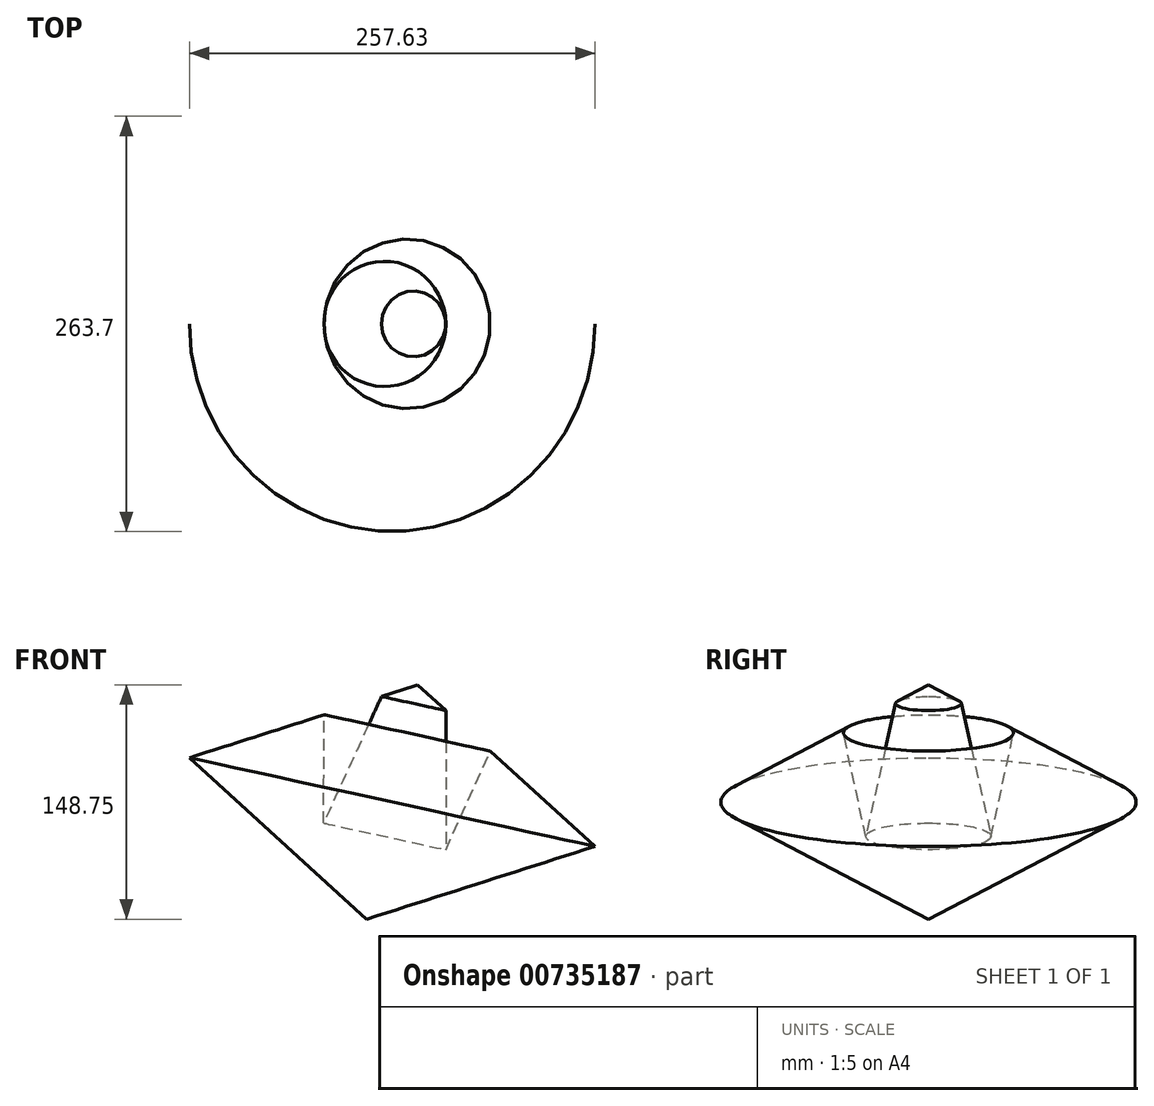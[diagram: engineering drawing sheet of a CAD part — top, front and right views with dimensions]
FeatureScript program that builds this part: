
annotation { "Feature Type Name" : "Feature", "Feature Type Description" : "" }
export const myFeature = defineFeature(function(context is Context, id is Id, definition is map)
    precondition{}
    {
        {
            var Q0;
            Q0=qCreatedBy(makeId("Front.planeOp"),FACE);
            var sketch = newSketch(context, id + "F0", { "sketchPlane" : qUnion([Q0])});
            skCircle(sketch, "E0.cCircle", {"center": v(0, 0) * mm, "radius": 43.95 * mm, "construction": true});
            skLineSegment(sketch, "E0.0", {"start": v(-26.68, 83.76) * mm, "end": v(-8.85, 67.51) * mm});
            skLineSegment(sketch, "E0.1", {"start": v(85.88, -18.77) * mm, "end": v(-59.2, -64.99) * mm});
            skLineSegment(sketch, "E0.2", {"start": v(-59.2, -64.99) * mm, "end": v(-26.68, 83.76) * mm});
            skPoint(sketch, "E0.0.midPoint", {"position": v(29.6, 32.5) * mm});
            skLineSegment(sketch, "E1", {"start": v(-8.85, 67.51) * mm, "end": v(-8.85, -20.9) * mm});
            skLineSegment(sketch, "E2", {"start": v(-8.85, -20.9) * mm, "end": v(19.37, 41.8) * mm});
            skLineSegment(sketch, "E3.trimOffspring", {"start": v(19.37, 41.8) * mm, "end": v(85.88, -18.77) * mm});
            skSolve(sketch);
        }
        {
            var Q0;
            Q0 = qSketchRegion(id + "F0", true);
            var Q1;
            Q1=sQuery(id+"F0.wireOp",EDGE,"E0.2");
            revolve(context, id + "F1", {"surfaceOperationType" : NewSurfaceOperationType.NEW, "entities" : qUnion([Q0]), "axis" : qUnion([Q1]), "revolveType" : RevolveType.FULL});
        }
    });
